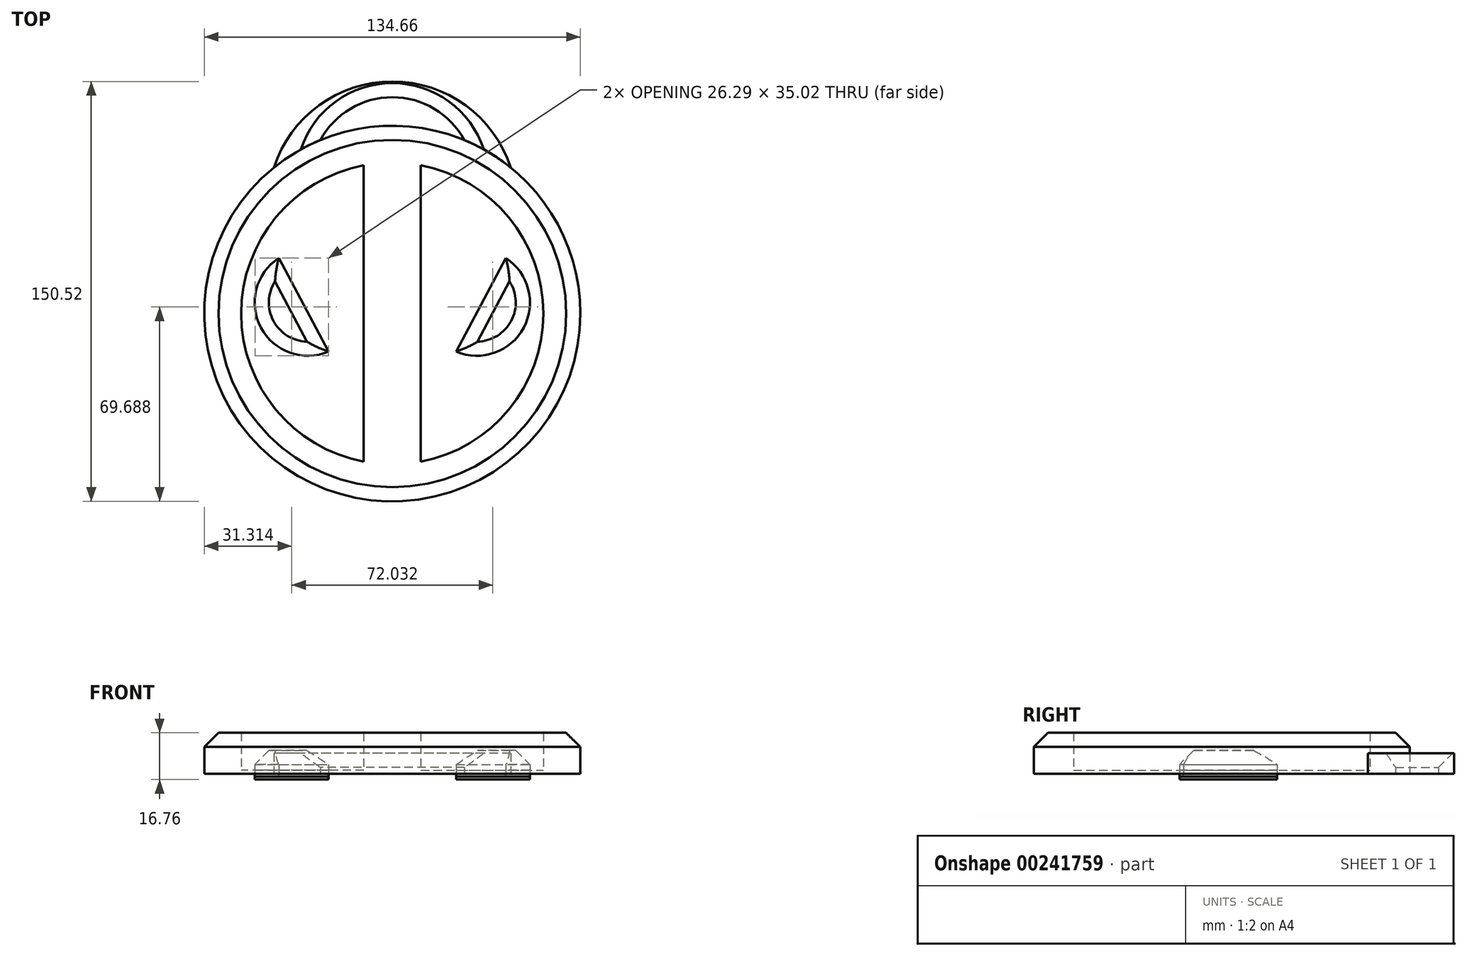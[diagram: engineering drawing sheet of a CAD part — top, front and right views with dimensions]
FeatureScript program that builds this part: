
annotation { "Feature Type Name" : "Feature", "Feature Type Description" : "" }
export const myFeature = defineFeature(function(context is Context, id is Id, definition is map)
    precondition{}
    {
        {
            var Q0;
            Q0=qCreatedBy(makeId("Top.planeOp"),FACE);
            var sketch = newSketch(context, id + "F0", { "sketchPlane" : qUnion([Q0])});
            skCircle(sketch, "E0", {"center": v(0, 0) * mm, "radius": 67.33 * mm});
            skArc(sketch, "E1", {"start": v(-10.21, 53.14) * mm, "mid": v(-54.11, 0) * mm, "end": v(-10.21, -53.14) * mm});
            skLineSegment(sketch, "E2.left", {"start": v(-10.21, -68.64) * mm, "end": v(-10.21, -66.55) * mm});
            skLineSegment(sketch, "E2.right", {"start": v(10.21, -68.64) * mm, "end": v(10.21, -66.55) * mm});
            skArc(sketch, "E3.trimOffspring", {"start": v(10.21, -53.14) * mm, "mid": v(54.11, 0) * mm, "end": v(10.21, 53.14) * mm});
            skLineSegment(sketch, "E4.trimOffspring", {"start": v(-10.21, -53.14) * mm, "end": v(-10.21, 53.14) * mm});
            skLineSegment(sketch, "E5.trimOffspring", {"start": v(10.21, -53.14) * mm, "end": v(10.21, 53.14) * mm});
            skLineSegment(sketch, "E6", {"start": v(22.87, -13.68) * mm, "end": v(40.68, 19.87) * mm});
            skArc(sketch, "E7", {"start": v(22.87, -13.68) * mm, "mid": v(47.07, -5.03) * mm, "end": v(40.68, 19.87) * mm});
            skLineSegment(sketch, "E8.MirrorCS", {"start": v(-22.87, -13.68) * mm, "end": v(-40.68, 19.87) * mm});
            skArc(sketch, "E9.MirrorCS", {"start": v(-22.87, -13.68) * mm, "mid": v(-47.07, -5.03) * mm, "end": v(-40.68, 19.87) * mm});
            skPoint(sketch, "E10.trimOffspring.end.orphan", {"position": v(10.21, 68.64) * mm});
            skPoint(sketch, "E11.trimOffspring.end.orphan", {"position": v(-10.21, 68.64) * mm});
            skPoint(sketch, "E12.center.orphan", {"position": v(0, 63.84) * mm});
            skPoint(sketch, "E13.center.orphan", {"position": v(0, 48.2) * mm});
            skPoint(sketch, "E14.center.orphan", {"position": v(0, 41.7) * mm});
            skPoint(sketch, "E15.center.orphan", {"position": v(0, 34.6) * mm});
            skArc(sketch, "E16", {"start": v(42.43, 52.28) * mm, "mid": v(0, 83.19) * mm, "end": v(-42.43, 52.28) * mm});
            skArc(sketch, "E17.trimOffspring", {"start": v(25.8, 62.2) * mm, "mid": v(0, 77.55) * mm, "end": v(-25.8, 62.2) * mm});
            skSolve(sketch);
        }
        {
            var Q0;
            Q0=makeQuery(id+"F0.imprint","IMPRINT",FACE,{"disambiguationData":[TD([[makeQuery(id+"F0.imprint","IMPRINT",EDGE,{"derivedFrom":sQuery(id+"F0.wireOp",EDGE,"E1")}),-1.0]])]});
            extrude(context, id + "F1", {"entities" : qUnion([Q0]), "depth" : 14.73 * mm});
        }
        {
            var Q0;
            Q0=makeQuery(id+"F0.imprint","IMPRINT",FACE,{"disambiguationData":[TD([[makeQuery(id+"F0.imprint","IMPRINT",EDGE,{"derivedFrom":sQuery(id+"F0.wireOp",EDGE,"E1")}),1.0]])]});
            var Q1;
            Q1=makeQuery(id+"F0.imprint","IMPRINT",FACE,{"disambiguationData":[TD([[makeQuery(id+"F0.imprint","IMPRINT",EDGE,{"derivedFrom":sQuery(id+"F0.wireOp",EDGE,"E3.trimOffspring")}),1.0]])]});
            extrude(context, id + "F2", {"entities" : qUnion([Q0, Q1]), "operationType" : NewBodyOperationType.ADD, "depth" : 1.27 * mm});
        }
        {
            var Q0;
            Q0=makeQuery(id+"F0.imprint","IMPRINT",FACE,{"disambiguationData":[TD([[makeQuery(id+"F0.imprint","IMPRINT",EDGE,{"derivedFrom":sQuery(id+"F0.wireOp",EDGE,"E8.MirrorCS")}),1.0]])]});
            var Q1;
            Q1=makeQuery(id+"F0.imprint","IMPRINT",FACE,{"disambiguationData":[TD([[makeQuery(id+"F0.imprint","IMPRINT",EDGE,{"derivedFrom":sQuery(id+"F0.wireOp",EDGE,"E6")}),-1.0]])]});
            extrude(context, id + "F3", {"entities" : qUnion([Q0, Q1]), "oppositeDirection" : true, "depth" : 2.03 * mm});
        }
        {
            var Q0;
            Q0=makeQuery(id+"F0.imprint","IMPRINT",FACE,{"disambiguationData":[TD([[makeQuery(id+"F0.imprint","IMPRINT",EDGE,{"derivedFrom":sQuery(id+"F0.wireOp",EDGE,"E8.MirrorCS")}),1.0]])]});
            var Q1;
            Q1=makeQuery(id+"F0.imprint","IMPRINT",FACE,{"disambiguationData":[TD([[makeQuery(id+"F0.imprint","IMPRINT",EDGE,{"derivedFrom":sQuery(id+"F0.wireOp",EDGE,"E6")}),-1.0]])]});
            extrude(context, id + "F4", {"entities" : qUnion([Q0, Q1]), "oppositeDirection" : true, "depth" : 1.02 * mm});
        }
        {
            var Q0;
            Q0=makeQuery(id+"F0.imprint","IMPRINT",FACE,{"disambiguationData":[TD([[makeQuery(id+"F0.imprint","IMPRINT",EDGE,{"derivedFrom":sQuery(id+"F0.wireOp",EDGE,"E6")}),-1.0]])]});
            var Q1;
            Q1=makeQuery(id+"F0.imprint","IMPRINT",FACE,{"disambiguationData":[TD([[makeQuery(id+"F0.imprint","IMPRINT",EDGE,{"derivedFrom":sQuery(id+"F0.wireOp",EDGE,"E8.MirrorCS")}),1.0]])]});
            extrude(context, id + "F5", {"entities" : qUnion([Q0, Q1]), "depth" : 8.38 * mm});
        }
        {
            var Q0;
            Q0=makeQuery(id+"F5.opExtrude","CAP_EDGE",EDGE,{"disambiguationData":[OSD([sQuery(id+"F0.wireOp",EDGE,"E8.MirrorCS")])],"isStart":false});
            var Q1;
            Q1=makeQuery(id+"F5.opExtrude","CAP_FACE",FACE,{"disambiguationData":[OSD([sQuery(id+"F0.wireOp",EDGE,"E8.MirrorCS"),sQuery(id+"F0.wireOp",EDGE,"E9.MirrorCS")])],"isStart":false});
            var Q2;
            Q2=makeQuery(id+"F5.opExtrude","CAP_FACE",FACE,{"disambiguationData":[OSD([sQuery(id+"F0.wireOp",EDGE,"E6"),sQuery(id+"F0.wireOp",EDGE,"E7")])],"isStart":false});
            chamfer(context, id + "F6", {"entities" : qUnion([Q0, Q1, Q2]), "width" : 5.08 * mm, "tangentPropagation" : true});
        }
        {
            var Q0;
            Q0=makeQuery(id+"F1.opExtrude","CAP_EDGE",EDGE,{"disambiguationData":[OSD([sQuery(id+"F0.wireOp",EDGE,"E0")])],"isStart":false});
            chamfer(context, id + "F7", {"entities" : qUnion([Q0]), "width" : 5.08 * mm, "tangentPropagation" : true});
        }
        {
            var Q0;
            {var subQ0=sQuery(id+"F0.wireOp",EDGE,"E16");Q0=makeQuery(id+"F0.imprint","IMPRINT",FACE,{"disambiguationData":[TD([[makeQuery(id+"F0.imprint","IMPRINT",EDGE,{"derivedFrom":subQ0}),1.0]])]});}
            extrude(context, id + "F8", {"entities" : qUnion([Q0]), "operationType" : NewBodyOperationType.ADD, "depth" : 7.37 * mm});
        }
        {
            var Q0;
            Q0=makeQuery(id+"F8.opExtrude","CAP_EDGE",EDGE,{"disambiguationData":[OSD([sQuery(id+"F0.wireOp",EDGE,"E17.trimOffspring")])],"isStart":false});
            chamfer(context, id + "F9", {"entities" : qUnion([Q0]), "width" : 5.08 * mm, "tangentPropagation" : true});
        }
    });
